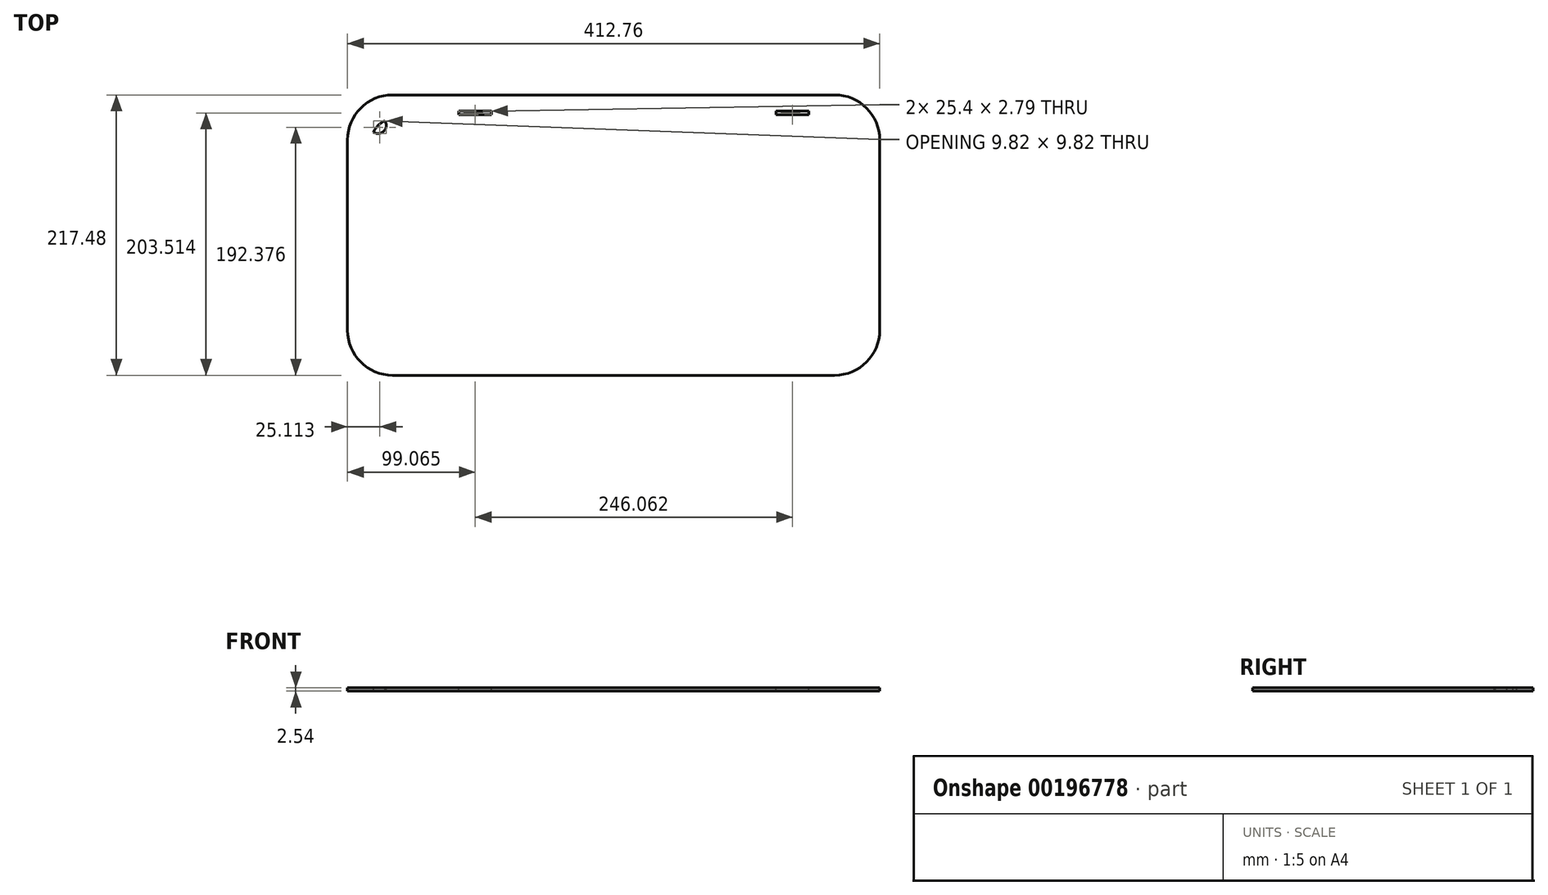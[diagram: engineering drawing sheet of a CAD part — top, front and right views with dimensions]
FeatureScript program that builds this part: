
annotation { "Feature Type Name" : "Feature", "Feature Type Description" : "" }
export const myFeature = defineFeature(function(context is Context, id is Id, definition is map)
    precondition{}
    {
        {
            var Q0;
            Q0=qCreatedBy(makeId("Top.planeOp"),FACE);
            var sketch = newSketch(context, id + "F0", { "sketchPlane" : qUnion([Q0])});
            skLineSegment(sketch, "E0.bottom", {"start": v(171.45, -89.7) * mm, "end": v(-171.45, -89.7) * mm});
            skLineSegment(sketch, "E0.top", {"start": v(171.45, 89.7) * mm, "end": v(-171.45, 89.7) * mm});
            skLineSegment(sketch, "E0.left", {"start": v(187.33, -73.82) * mm, "end": v(187.33, 73.82) * mm});
            skLineSegment(sketch, "E0.right", {"start": v(-187.32, -73.82) * mm, "end": v(-187.33, 73.82) * mm});
            skPoint(sketch, "E0.middle", {"position": v(0, 0) * mm});
            skPoint(sketch, "E1.visualSharp", {"position": v(-187.33, 89.7) * mm});
            skArc(sketch, "E1.filletArc", {"start": v(-171.45, 89.7) * mm, "mid": v(-182.68, 85.04) * mm, "end": v(-187.33, 73.82) * mm});
            skPoint(sketch, "E2.visualSharp", {"position": v(-187.33, -89.7) * mm});
            skArc(sketch, "E2.filletArc", {"start": v(-187.32, -73.82) * mm, "mid": v(-182.68, -85.04) * mm, "end": v(-171.45, -89.7) * mm});
            skPoint(sketch, "E3.visualSharp", {"position": v(187.33, -89.7) * mm});
            skArc(sketch, "E3.filletArc", {"start": v(171.45, -89.7) * mm, "mid": v(182.68, -85.04) * mm, "end": v(187.33, -73.82) * mm});
            skPoint(sketch, "E4.visualSharp", {"position": v(187.33, 89.7) * mm});
            skArc(sketch, "E4.filletArc", {"start": v(187.33, 73.82) * mm, "mid": v(182.68, 85.04) * mm, "end": v(171.45, 89.7) * mm});
            skArc(sketch, "E5.0", {"start": v(206.38, 73.82) * mm, "mid": v(196.15, 98.51) * mm, "end": v(171.45, 108.74) * mm});
            skLineSegment(sketch, "E5.1", {"start": v(206.38, -73.82) * mm, "end": v(206.38, 73.82) * mm});
            skLineSegment(sketch, "E5.2", {"start": v(171.45, 108.74) * mm, "end": v(-171.45, 108.74) * mm});
            skArc(sketch, "E5.3", {"start": v(171.45, -108.74) * mm, "mid": v(196.15, -98.51) * mm, "end": v(206.38, -73.82) * mm});
            skArc(sketch, "E5.4", {"start": v(-171.45, 108.74) * mm, "mid": v(-196.15, 98.51) * mm, "end": v(-206.38, 73.82) * mm});
            skLineSegment(sketch, "E5.5", {"start": v(-206.38, -73.82) * mm, "end": v(-206.38, 73.82) * mm});
            skArc(sketch, "E5.6", {"start": v(-206.37, -73.82) * mm, "mid": v(-196.15, -98.51) * mm, "end": v(-171.45, -108.74) * mm});
            skLineSegment(sketch, "E5.7", {"start": v(171.45, -108.74) * mm, "end": v(-171.45, -108.74) * mm});
            skSolve(sketch);
        }
        {
            var Q0;
            Q0=qSketchRegion(id+"F0",true);
            extrude(context, id + "F1", {"entities" : qUnion([Q0]), "depth" : 2.54 * mm});
        }
        {
            var Q0;
            Q0=makeQuery(id+"F1.opExtrude","CAP_FACE",FACE,{"disambiguationData":[OSD([sQuery(id+"F0.wireOp",EDGE,"E0.bottom"),sQuery(id+"F0.wireOp",EDGE,"E0.top"),sQuery(id+"F0.wireOp",EDGE,"E0.left"),sQuery(id+"F0.wireOp",EDGE,"E0.right"),sQuery(id+"F0.wireOp",EDGE,"E1.filletArc"),sQuery(id+"F0.wireOp",EDGE,"E2.filletArc"),sQuery(id+"F0.wireOp",EDGE,"E3.filletArc"),sQuery(id+"F0.wireOp",EDGE,"E4.filletArc"),sQuery(id+"F0.wireOp",EDGE,"E5.0"),sQuery(id+"F0.wireOp",EDGE,"E5.1"),sQuery(id+"F0.wireOp",EDGE,"E5.2"),sQuery(id+"F0.wireOp",EDGE,"E5.3"),sQuery(id+"F0.wireOp",EDGE,"E5.4"),sQuery(id+"F0.wireOp",EDGE,"E5.5"),sQuery(id+"F0.wireOp",EDGE,"E5.6"),sQuery(id+"F0.wireOp",EDGE,"E5.7")])],"isStart":false});
            var sketch = newSketch(context, id + "F2", { "sketchPlane" : qUnion([Q0])});
            skLineSegment(sketch, "E6.bottom", {"start": v(-136.53, 89.7) * mm, "end": v(-126.37, 89.7) * mm});
            skLineSegment(sketch, "E6.top", {"start": v(-136.53, 99.85) * mm, "end": v(-126.37, 99.85) * mm});
            skLineSegment(sketch, "E6.left", {"start": v(-136.53, 89.7) * mm, "end": v(-136.53, 99.85) * mm});
            skLineSegment(sketch, "E6.right", {"start": v(-126.37, 89.7) * mm, "end": v(-126.37, 99.85) * mm});
            skLineSegment(sketch, "E7.bottom", {"start": v(109.54, 89.7) * mm, "end": v(119.7, 89.7) * mm});
            skLineSegment(sketch, "E7.top", {"start": v(109.54, 99.85) * mm, "end": v(119.7, 99.85) * mm});
            skLineSegment(sketch, "E7.left", {"start": v(109.54, 89.7) * mm, "end": v(109.54, 99.85) * mm});
            skLineSegment(sketch, "E7.right", {"start": v(119.7, 89.7) * mm, "end": v(119.7, 99.85) * mm});
            skSolve(sketch);
        }
        {
            var Q0;
            Q0=qSketchRegion(id+"F2",true);
            extrude(context, id + "F3", {"entities" : qUnion([Q0]), "operationType" : NewBodyOperationType.REMOVE, "endBound" : BoundingType.UP_TO_NEXT, "oppositeDirection" : true, "depth" : 25.4 * mm});
        }
        {
            var Q0;
            Q0=makeQuery(id+"F1.opExtrude","CAP_FACE",FACE,{"disambiguationData":[OSD([sQuery(id+"F0.wireOp",EDGE,"E0.bottom"),sQuery(id+"F0.wireOp",EDGE,"E0.top"),sQuery(id+"F0.wireOp",EDGE,"E0.left"),sQuery(id+"F0.wireOp",EDGE,"E0.right"),sQuery(id+"F0.wireOp",EDGE,"E1.filletArc"),sQuery(id+"F0.wireOp",EDGE,"E2.filletArc"),sQuery(id+"F0.wireOp",EDGE,"E3.filletArc"),sQuery(id+"F0.wireOp",EDGE,"E4.filletArc"),sQuery(id+"F0.wireOp",EDGE,"E5.0"),sQuery(id+"F0.wireOp",EDGE,"E5.1"),sQuery(id+"F0.wireOp",EDGE,"E5.2"),sQuery(id+"F0.wireOp",EDGE,"E5.3"),sQuery(id+"F0.wireOp",EDGE,"E5.4"),sQuery(id+"F0.wireOp",EDGE,"E5.5"),sQuery(id+"F0.wireOp",EDGE,"E5.6"),sQuery(id+"F0.wireOp",EDGE,"E5.7")])],"isStart":false});
            var sketch = newSketch(context, id + "F4", { "sketchPlane" : qUnion([Q0])});
            skArc(sketch, "E8", {"start": v(-177.38, 88.55) * mm, "mid": v(-178.19, 80.55) * mm, "end": v(-186.18, 79.75) * mm});
            skArc(sketch, "E9", {"start": v(177.38, 88.55) * mm, "mid": v(178.19, 80.55) * mm, "end": v(186.18, 79.75) * mm});
            skArc(sketch, "E10", {"start": v(186.18, -79.75) * mm, "mid": v(178.19, -80.55) * mm, "end": v(177.38, -88.55) * mm});
            skArc(sketch, "E11", {"start": v(-177.38, -88.55) * mm, "mid": v(-178.19, -80.55) * mm, "end": v(-186.18, -79.75) * mm});
            skSolve(sketch);
        }
        {
            var Q0;
            {var subQ0=sQuery(id+"F4.wireOp",EDGE,"E8");Q0=makeQuery(id+"F4.imprint","IMPRINT",FACE,{"disambiguationData":[TD([[makeQuery(id+"F4.imprint","IMPRINT",EDGE,{"derivedFrom":subQ0}),-1.0]])]});}
            var Q1;
            {var subQ0=sQuery(id+"F4.wireOp",EDGE,"E9");Q1=makeQuery(id+"F4.imprint","IMPRINT",FACE,{"disambiguationData":[TD([[makeQuery(id+"F4.imprint","IMPRINT",EDGE,{"derivedFrom":subQ0}),1.0]])]});}
            var Q2;
            {var subQ0=sQuery(id+"F4.wireOp",EDGE,"E10");Q2=makeQuery(id+"F4.imprint","IMPRINT",FACE,{"disambiguationData":[TD([[makeQuery(id+"F4.imprint","IMPRINT",EDGE,{"derivedFrom":subQ0}),1.0]])]});}
            var Q3;
            {var subQ0=sQuery(id+"F4.wireOp",EDGE,"E11");Q3=makeQuery(id+"F4.imprint","IMPRINT",FACE,{"disambiguationData":[TD([[makeQuery(id+"F4.imprint","IMPRINT",EDGE,{"derivedFrom":subQ0}),1.0]])]});}
            var Q4;
            Q4=makeQuery(id+"F1.opExtrude","CAP_FACE",FACE,{"disambiguationData":[OSD([sQuery(id+"F0.wireOp",EDGE,"E0.bottom"),sQuery(id+"F0.wireOp",EDGE,"E0.top"),sQuery(id+"F0.wireOp",EDGE,"E0.left"),sQuery(id+"F0.wireOp",EDGE,"E0.right"),sQuery(id+"F0.wireOp",EDGE,"E1.filletArc"),sQuery(id+"F0.wireOp",EDGE,"E2.filletArc"),sQuery(id+"F0.wireOp",EDGE,"E3.filletArc"),sQuery(id+"F0.wireOp",EDGE,"E4.filletArc"),sQuery(id+"F0.wireOp",EDGE,"E5.0"),sQuery(id+"F0.wireOp",EDGE,"E5.1"),sQuery(id+"F0.wireOp",EDGE,"E5.2"),sQuery(id+"F0.wireOp",EDGE,"E5.3"),sQuery(id+"F0.wireOp",EDGE,"E5.4"),sQuery(id+"F0.wireOp",EDGE,"E5.5"),sQuery(id+"F0.wireOp",EDGE,"E5.6"),sQuery(id+"F0.wireOp",EDGE,"E5.7")])],"isStart":true});
            extrude(context, id + "F5", {"entities" : qUnion([Q0, Q1, Q2, Q3]), "operationType" : NewBodyOperationType.ADD, "endBound" : BoundingType.UP_TO_SURFACE, "oppositeDirection" : true, "endBoundEntityFace" : qUnion([Q4]), "depth" : 25.4 * mm});
        }
        {
            var Q0;
            {var subQ0=sQuery(id+"F0.wireOp",EDGE,"E2.filletArc");var subQ1=sQuery(id+"F0.wireOp",EDGE,"E3.filletArc");var subQ2=sQuery(id+"F0.wireOp",EDGE,"E4.filletArc");var subQ3=sQuery(id+"F0.wireOp",EDGE,"E1.filletArc");Q0=makeQuery(id+"F5.boolean.opBoolean","MERGE",FACE,{"derivedFrom":[makeQuery(id+"F1.opExtrude","CAP_FACE",FACE,{"disambiguationData":[OSD([sQuery(id+"F0.wireOp",EDGE,"E0.bottom"),sQuery(id+"F0.wireOp",EDGE,"E0.top"),sQuery(id+"F0.wireOp",EDGE,"E0.left"),sQuery(id+"F0.wireOp",EDGE,"E0.right"),subQ3,subQ0,subQ1,subQ2,sQuery(id+"F0.wireOp",EDGE,"E5.0"),sQuery(id+"F0.wireOp",EDGE,"E5.1"),sQuery(id+"F0.wireOp",EDGE,"E5.2"),sQuery(id+"F0.wireOp",EDGE,"E5.3"),sQuery(id+"F0.wireOp",EDGE,"E5.4"),sQuery(id+"F0.wireOp",EDGE,"E5.5"),sQuery(id+"F0.wireOp",EDGE,"E5.6"),sQuery(id+"F0.wireOp",EDGE,"E5.7")])],"isStart":false}),makeQuery(id+"F5.opExtrude","CAP_FACE",FACE,{"disambiguationData":[OSD([subQ3,sQuery(id+"F4.wireOp",EDGE,"E8")])],"isStart":true}),makeQuery(id+"F5.opExtrude","CAP_FACE",FACE,{"disambiguationData":[OSD([subQ2,sQuery(id+"F4.wireOp",EDGE,"E9")])],"isStart":true}),makeQuery(id+"F5.opExtrude","CAP_FACE",FACE,{"disambiguationData":[OSD([subQ1,sQuery(id+"F4.wireOp",EDGE,"E10")])],"isStart":true}),makeQuery(id+"F5.opExtrude","CAP_FACE",FACE,{"disambiguationData":[OSD([subQ0,sQuery(id+"F4.wireOp",EDGE,"E11")])],"isStart":true})]});}
            var sketch = newSketch(context, id + "F6", { "sketchPlane" : qUnion([Q0])});
            skLineSegment(sketch, "E12", {"start": v(-126.37, 94.77) * mm, "end": v(199.4, 94.77) * mm, "construction": true});
            skLineSegment(sketch, "E13.bottom", {"start": v(-94.62, 96.17) * mm, "end": v(-120.02, 96.17) * mm});
            skLineSegment(sketch, "E13.top", {"start": v(-94.62, 93.38) * mm, "end": v(-120.02, 93.38) * mm});
            skLineSegment(sketch, "E13.left", {"start": v(-94.62, 96.17) * mm, "end": v(-94.62, 93.38) * mm});
            skLineSegment(sketch, "E13.right", {"start": v(-120.02, 96.17) * mm, "end": v(-120.02, 93.38) * mm});
            skPoint(sketch, "E13.middle", {"position": v(-107.32, 94.77) * mm});
            skLineSegment(sketch, "E14.bottom", {"start": v(151.45, 96.17) * mm, "end": v(126.05, 96.17) * mm});
            skLineSegment(sketch, "E14.top", {"start": v(151.45, 93.38) * mm, "end": v(126.05, 93.38) * mm});
            skLineSegment(sketch, "E14.left", {"start": v(151.45, 96.17) * mm, "end": v(151.45, 93.38) * mm});
            skLineSegment(sketch, "E14.right", {"start": v(126.05, 96.17) * mm, "end": v(126.05, 93.38) * mm});
            skPoint(sketch, "E14.middle", {"position": v(138.75, 94.77) * mm});
            skSolve(sketch);
        }
        {
            var Q0;
            Q0 = qSketchRegion(id + "F6", true);
            extrude(context, id + "F7", {"entities" : qUnion([Q0]), "operationType" : NewBodyOperationType.REMOVE, "oppositeDirection" : true, "depth" : 25.4 * mm});
        }
    });
